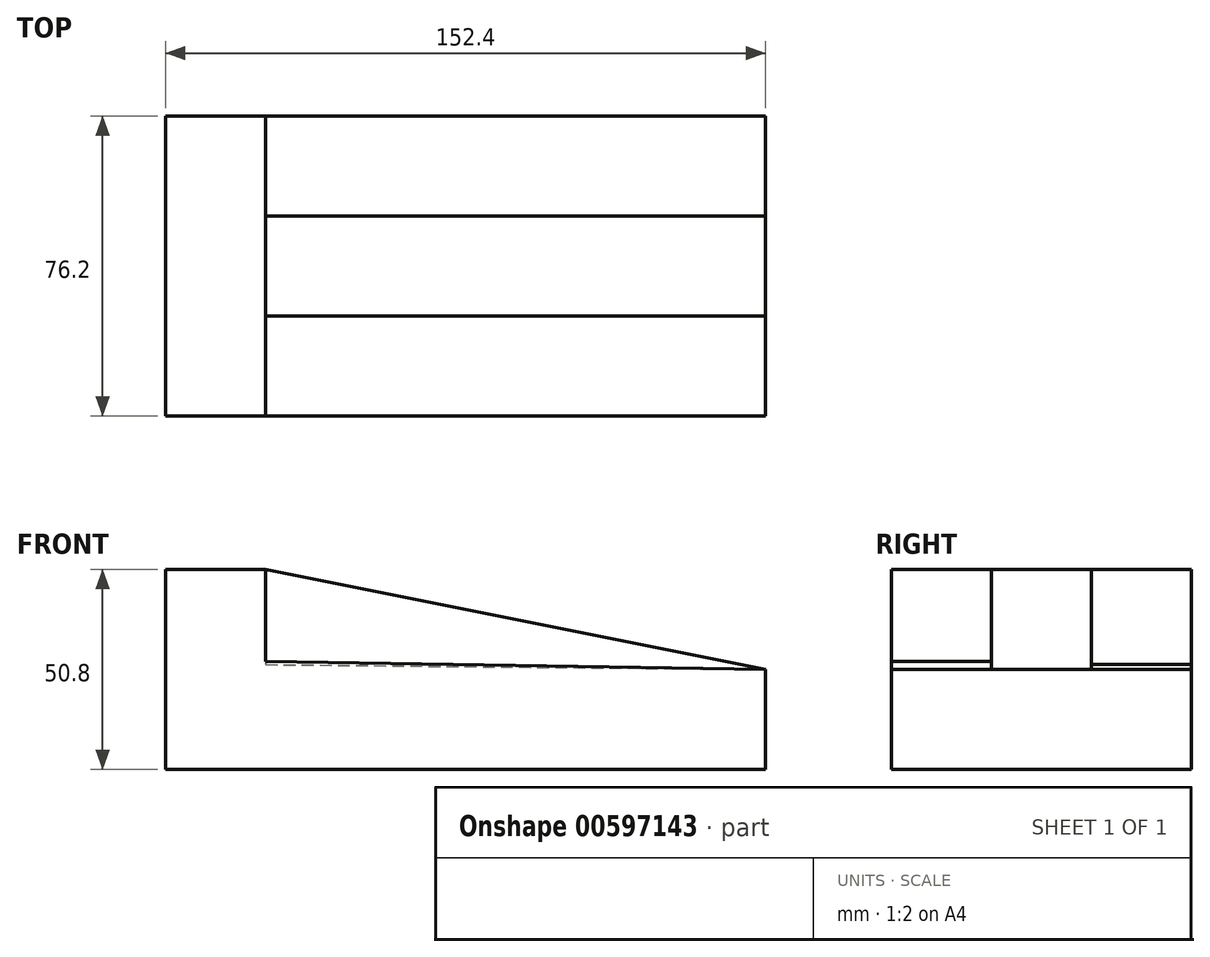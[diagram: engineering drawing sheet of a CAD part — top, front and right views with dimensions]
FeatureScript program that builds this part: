
annotation { "Feature Type Name" : "Feature", "Feature Type Description" : "" }
export const myFeature = defineFeature(function(context is Context, id is Id, definition is map)
    precondition{}
    {
        {
            var Q0;
            Q0=qCreatedBy(makeId("Front.planeOp"),FACE);
            var sketch = newSketch(context, id + "F0", { "sketchPlane" : qUnion([Q0])});
            skLineSegment(sketch, "E0", {"start": v(0, 0) * mm, "end": v(0, 50.8) * mm});
            skLineSegment(sketch, "E1", {"start": v(0, 50.8) * mm, "end": v(25.4, 50.8) * mm});
            skLineSegment(sketch, "E2", {"start": v(25.4, 50.8) * mm, "end": v(25.4, 25.4) * mm});
            skLineSegment(sketch, "E3", {"start": v(25.4, 25.4) * mm, "end": v(152.4, 25.4) * mm});
            skLineSegment(sketch, "E4", {"start": v(152.4, 25.4) * mm, "end": v(152.4, 0) * mm});
            skLineSegment(sketch, "E5", {"start": v(152.4, 0) * mm, "end": v(0, 0) * mm});
            skSolve(sketch);
        }
        {
            var Q0;
            Q0=makeQuery(id+"F0.imprint","IMPRINT",FACE,{"disambiguationData":[TD([[makeQuery(id+"F0.imprint","IMPRINT",EDGE,{"derivedFrom":sQuery(id+"F0.wireOp",EDGE,"E0")}),-1.0]])]});
            extrude(context, id + "F1", {"entities" : qUnion([Q0]), "oppositeDirection" : true, "depth" : 76.2 * mm, "offsetDistance" : 25.4 * mm});
        }
        {
            var Q0;
            Q0=makeQuery(id+"F1.opExtrude","CAP_FACE",FACE,{"disambiguationData":[OSD([sQuery(id+"F0.wireOp",EDGE,"E0"),sQuery(id+"F0.wireOp",EDGE,"E1"),sQuery(id+"F0.wireOp",EDGE,"E2"),sQuery(id+"F0.wireOp",EDGE,"E3"),sQuery(id+"F0.wireOp",EDGE,"E4"),sQuery(id+"F0.wireOp",EDGE,"E5")])],"isStart":true});
            var sketch = newSketch(context, id + "F2", { "sketchPlane" : qUnion([Q0])});
            skLineSegment(sketch, "E6", {"start": v(25.4, 50.8) * mm, "end": v(25.4, 25.4) * mm});
            skLineSegment(sketch, "E7", {"start": v(25.4, 25.4) * mm, "end": v(152.4, 25.4) * mm});
            skLineSegment(sketch, "E8", {"start": v(152.4, 25.4) * mm, "end": v(25.4, 50.8) * mm});
            skSolve(sketch);
        }
        {
            var Q0;
            Q0=makeQuery(id+"F2.imprint","IMPRINT",FACE,{"disambiguationData":[TD([[makeQuery(id+"F2.imprint","IMPRINT",EDGE,{"derivedFrom":sQuery(id+"F2.wireOp",EDGE,"E6")}),1.0]])]});
            extrude(context, id + "F3", {"entities" : qUnion([Q0]), "operationType" : NewBodyOperationType.ADD, "oppositeDirection" : true, "depth" : 76.2 * mm, "offsetDistance" : 25.4 * mm});
        }
        {
            var Q0;
            Q0=makeQuery(id+"F3.boolean.opBoolean","MERGE",FACE,{"derivedFrom":[makeQuery(id+"F1.opExtrude","CAP_FACE",FACE,{"disambiguationData":[OSD([sQuery(id+"F0.wireOp",EDGE,"E0"),sQuery(id+"F0.wireOp",EDGE,"E1"),sQuery(id+"F0.wireOp",EDGE,"E2"),sQuery(id+"F0.wireOp",EDGE,"E3"),sQuery(id+"F0.wireOp",EDGE,"E4"),sQuery(id+"F0.wireOp",EDGE,"E5")])],"isStart":true}),makeQuery(id+"F3.opExtrude","CAP_FACE",FACE,{"disambiguationData":[OSD([sQuery(id+"F2.wireOp",EDGE,"E6"),sQuery(id+"F2.wireOp",EDGE,"E7"),sQuery(id+"F2.wireOp",EDGE,"E8")])],"isStart":true})]});
            var sketch = newSketch(context, id + "F4", { "sketchPlane" : qUnion([Q0])});
            skLineSegment(sketch, "E9", {"start": v(25.4, 50.8) * mm, "end": v(25.4, 27.4) * mm});
            skLineSegment(sketch, "E10", {"start": v(25.4, 27.4) * mm, "end": v(152.4, 25.4) * mm});
            skSolve(sketch);
        }
        {
            var Q0;
            Q0=makeQuery(id+"F4.imprint","IMPRINT",FACE,{"disambiguationData":[TD([[makeQuery(id+"F4.imprint","IMPRINT",EDGE,{"derivedFrom":sQuery(id+"F4.wireOp",EDGE,"E9")}),1.0]])]});
            extrude(context, id + "F5", {"entities" : qUnion([Q0]), "operationType" : NewBodyOperationType.REMOVE, "oppositeDirection" : true, "depth" : 25.4 * mm, "offsetDistance" : 25.4 * mm});
        }
        {
            var Q0;
            Q0=makeQuery(id+"F3.boolean.opBoolean","MERGE",FACE,{"derivedFrom":[makeQuery(id+"F1.opExtrude","CAP_FACE",FACE,{"disambiguationData":[OSD([sQuery(id+"F0.wireOp",EDGE,"E0"),sQuery(id+"F0.wireOp",EDGE,"E1"),sQuery(id+"F0.wireOp",EDGE,"E2"),sQuery(id+"F0.wireOp",EDGE,"E3"),sQuery(id+"F0.wireOp",EDGE,"E4"),sQuery(id+"F0.wireOp",EDGE,"E5")])],"isStart":false}),makeQuery(id+"F3.opExtrude","CAP_FACE",FACE,{"disambiguationData":[OSD([sQuery(id+"F2.wireOp",EDGE,"E6"),sQuery(id+"F2.wireOp",EDGE,"E7"),sQuery(id+"F2.wireOp",EDGE,"E8")])],"isStart":false})]});
            var sketch = newSketch(context, id + "F6", { "sketchPlane" : qUnion([Q0])});
            skLineSegment(sketch, "E11", {"start": v(-25.4, 50.8) * mm, "end": v(-25.4, 26.63) * mm});
            skLineSegment(sketch, "E12", {"start": v(-25.4, 26.63) * mm, "end": v(-152.4, 25.4) * mm});
            skSolve(sketch);
        }
        {
            var Q0;
            Q0=makeQuery(id+"F6.imprint","IMPRINT",FACE,{"disambiguationData":[TD([[makeQuery(id+"F6.imprint","IMPRINT",EDGE,{"derivedFrom":sQuery(id+"F6.wireOp",EDGE,"E11")}),-1.0]])]});
            extrude(context, id + "F7", {"entities" : qUnion([Q0]), "operationType" : NewBodyOperationType.REMOVE, "oppositeDirection" : true, "depth" : 25.4 * mm, "offsetDistance" : 25.4 * mm});
        }
    });
